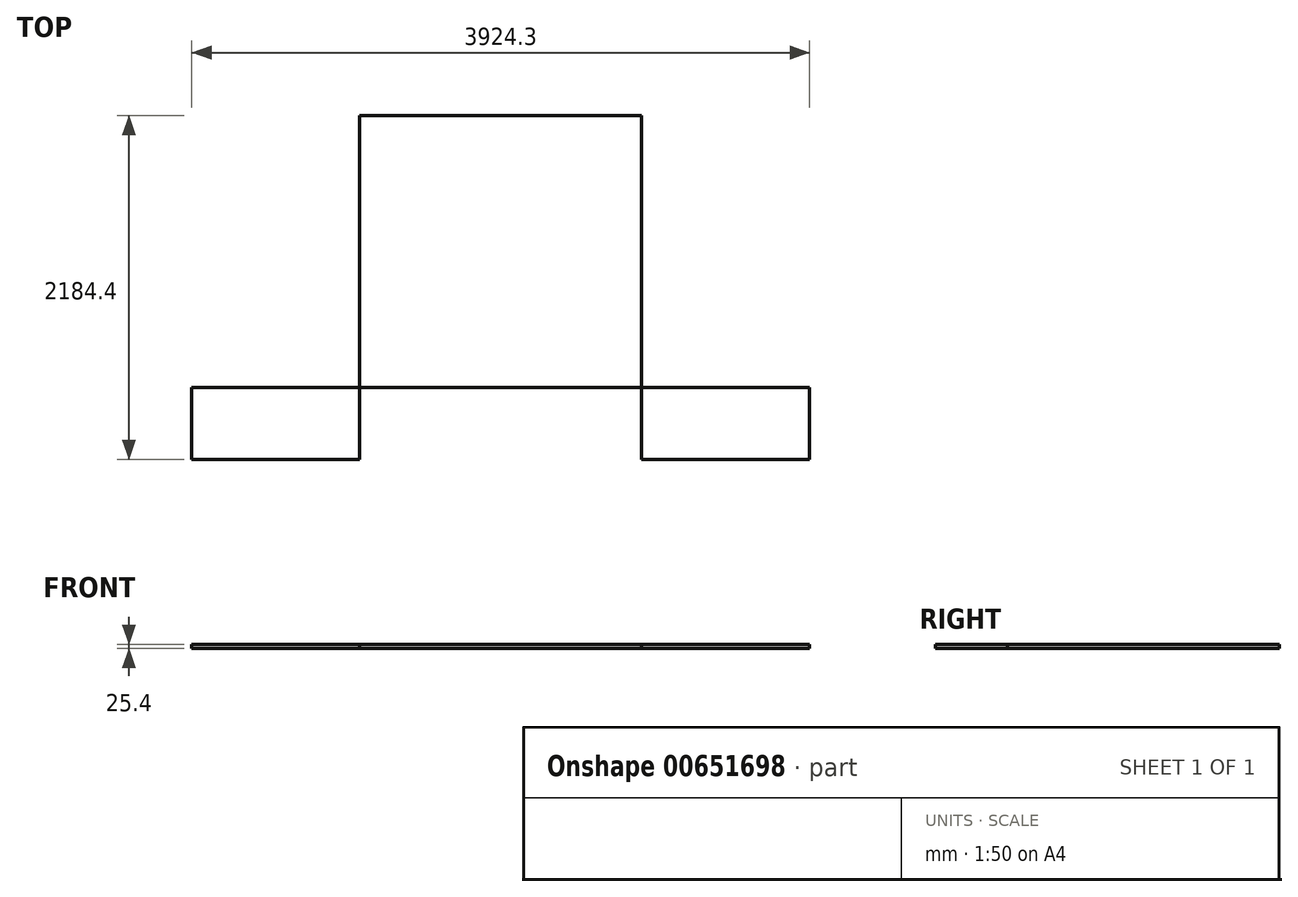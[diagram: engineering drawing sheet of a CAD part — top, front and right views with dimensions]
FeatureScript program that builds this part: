
annotation { "Feature Type Name" : "Feature", "Feature Type Description" : "" }
export const myFeature = defineFeature(function(context is Context, id is Id, definition is map)
    precondition{}
    {
        {
            var Q0;
            Q0=qCreatedBy(makeId("Top.planeOp"),FACE);
            var sketch = newSketch(context, id + "F0", { "sketchPlane" : qUnion([Q0])});
            skLineSegment(sketch, "E0.bottom", {"start": v(-395.15, 1114.09) * mm, "end": v(1395.55, 1114.09) * mm});
            skLineSegment(sketch, "E0.top", {"start": v(-395.15, -613.11) * mm, "end": v(1395.55, -613.11) * mm});
            skLineSegment(sketch, "E0.left", {"start": v(-395.15, 1114.09) * mm, "end": v(-395.15, -613.11) * mm});
            skLineSegment(sketch, "E0.right", {"start": v(1395.55, 1114.09) * mm, "end": v(1395.55, -613.11) * mm});
            skLineSegment(sketch, "E1.bottom", {"start": v(-395.15, -613.11) * mm, "end": v(-1461.95, -613.11) * mm});
            skLineSegment(sketch, "E1.top", {"start": v(-395.15, -1070.31) * mm, "end": v(-1461.95, -1070.31) * mm});
            skLineSegment(sketch, "E1.left", {"start": v(-395.15, -613.11) * mm, "end": v(-395.15, -1070.31) * mm});
            skLineSegment(sketch, "E1.right", {"start": v(-1461.95, -613.11) * mm, "end": v(-1461.95, -1070.31) * mm});
            skLineSegment(sketch, "E2.bottom", {"start": v(1395.55, -613.11) * mm, "end": v(2462.35, -613.11) * mm});
            skLineSegment(sketch, "E2.top", {"start": v(1395.55, -1070.31) * mm, "end": v(2462.35, -1070.31) * mm});
            skLineSegment(sketch, "E2.left", {"start": v(1395.55, -613.11) * mm, "end": v(1395.55, -1070.31) * mm});
            skLineSegment(sketch, "E2.right", {"start": v(2462.35, -613.11) * mm, "end": v(2462.35, -1070.31) * mm});
            skSolve(sketch);
        }
        {
            var Q0;
            Q0 = qSketchRegion(id + "F0", true);
            extrude(context, id + "F1", {"entities" : qUnion([Q0]), "depth" : 25.4 * mm, "offsetDistance" : 25.4 * mm});
        }
    });
